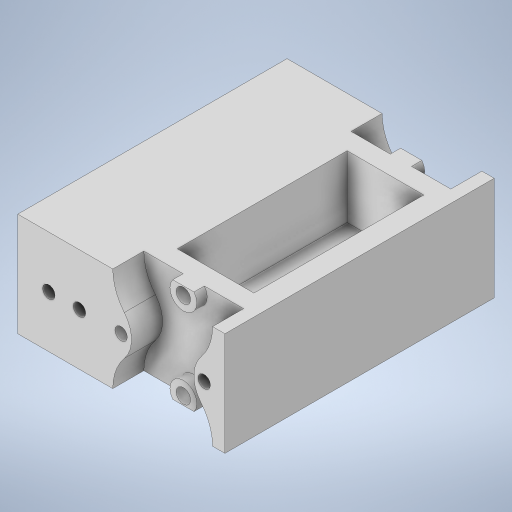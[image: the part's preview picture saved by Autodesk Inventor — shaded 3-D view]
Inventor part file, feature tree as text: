
AUTODESK INVENTOR PART (.ipt)
format: ipt  version: 2024 (Build 280153000, 153)  size: 364,544 bytes
history: native  units: in
note: dims shown in document units (in); Inventor stores cm internally (conversion verified against a paired STEP export)
features: extrude x6, sketch x6, projected_geometry x6, mirror x3, plane x2
ambient origin geometry x8: Origin, YZ Plane, XZ Plane, XY Plane, X Axis, Y Axis, Z Axis, Center Point
bodies: Solid1 (feature_tree)
feature tree (23):
  extrude  "Extrusion1"  Depth=3.937in
  extrude  "Extrusion2"  Depth=3.2283in
  extrude  "Extrusion3"  Depth=0.3937in
  plane  "Work Plane1"
  plane  "Work Plane2"
  extrude  "Extrusion4"  Depth=1.6535in
  mirror  "Mirror1"
  extrude  "Extrusion5"  Depth=0.1575in
  mirror  "Mirror2"
  extrude  "Extrusion6"  Depth=1.1811in
  mirror  "Mirror3"
  sketch  "Sketch1"  dims[d0=5.1181in d1=3.937in]
  sketch  "Sketch2"  dims[d2=1.9685in d3=0.0in d4=3.2283in]
  projected_geometry  "Projected Loop1"
  sketch  "Sketch3"  dims[d5=1.4567in d6=0.3937in]
  projected_geometry  "Projected Loop2"
  sketch  "Sketch5"  dims[d7=1.1811in d8=0.0in d9=1.6535in]
  projected_geometry  "Projected Loop4"
  sketch  "Sketch6"  dims[d10=3.7402in d11=0.1575in]
  projected_geometry  "Projected Loop5"
  sketch  "Sketch7"  dims[d12=1.063in d13=0.0in d14=1.1811in d15=2.3661in d16=0.5906in d17=0.0in d18=0.5118in d19=1.6535in d20=0.8268in d21=0.2756in d22=0.1969in d23=0.0in d24=0.2362in d25=0.2362in d26=1.5787in d27=0.7894in d28=0.3937in d29=0.0in d30=0.7913in d31=0.5827in]
  projected_geometry  "Projected Loop6"
  projected_geometry  "Projected Loop7"
